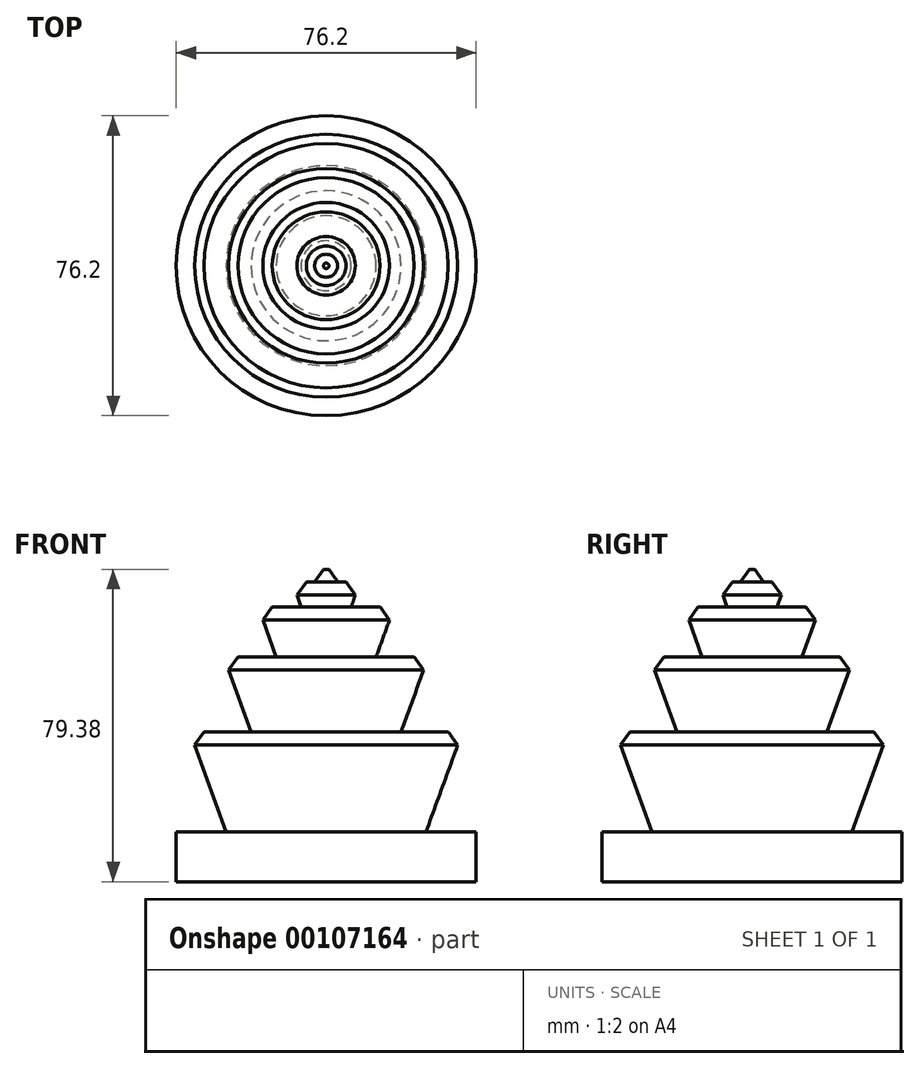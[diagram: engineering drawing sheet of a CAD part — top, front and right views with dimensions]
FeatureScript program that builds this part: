
annotation { "Feature Type Name" : "Feature", "Feature Type Description" : "" }
export const myFeature = defineFeature(function(context is Context, id is Id, definition is map)
    precondition{}
    {
        {
            var Q0;
            Q0=qCreatedBy(makeId("Top.planeOp"),FACE);
            var sketch = newSketch(context, id + "F0", { "sketchPlane" : qUnion([Q0])});
            skCircle(sketch, "E0", {"center": v(0, 0) * mm, "radius": 38.1 * mm});
            skSolve(sketch);
        }
        {
            var Q0;
            Q0 = qSketchRegion(id + "F0", true);
            extrude(context, id + "F1", {"entities" : qUnion([Q0]), "depth" : 12.7 * mm});
        }
        {
            var Q0;
            Q0=makeQuery(id+"F1.opExtrude","CAP_FACE",FACE,{"disambiguationData":[OSD([sQuery(id+"F0.wireOp",EDGE,"E0")])],"isStart":false});
            var sketch = newSketch(context, id + "F2", { "sketchPlane" : qUnion([Q0])});
            skCircle(sketch, "E1", {"center": v(0, 0) * mm, "radius": 25.4 * mm});
            skSolve(sketch);
        }
        {
            var Q0;
            Q0 = qSketchRegion(id + "F2", true);
            extrude(context, id + "F3", {"entities" : qUnion([Q0]), "operationType" : NewBodyOperationType.ADD, "depth" : 25.4 * mm, "hasDraft" : true, "draftAngle" : 20 * degree});
        }
        {
            var Q0;
            Q0=makeQuery(id+"F3.opExtrude","CAP_FACE",FACE,{"disambiguationData":[OSD([sQuery(id+"F2.wireOp",EDGE,"E1")])],"isStart":false});
            var sketch = newSketch(context, id + "F4", { "sketchPlane" : qUnion([Q0])});
            skCircle(sketch, "E2", {"center": v(0, 0) * mm, "radius": 19.05 * mm});
            skSolve(sketch);
        }
        {
            var Q0;
            Q0 = qSketchRegion(id + "F4", true);
            extrude(context, id + "F5", {"entities" : qUnion([Q0]), "operationType" : NewBodyOperationType.ADD, "depth" : 19.05 * mm, "hasDraft" : true, "draftAngle" : 20 * degree});
        }
        {
            var Q0;
            Q0=makeQuery(id+"F5.opExtrude","CAP_FACE",FACE,{"disambiguationData":[OSD([sQuery(id+"F4.wireOp",EDGE,"E2")])],"isStart":false});
            var sketch = newSketch(context, id + "F6", { "sketchPlane" : qUnion([Q0])});
            skCircle(sketch, "E3", {"center": v(0, 0) * mm, "radius": 12.7 * mm});
            skSolve(sketch);
        }
        {
            var Q0;
            Q0 = qSketchRegion(id + "F6", true);
            extrude(context, id + "F7", {"entities" : qUnion([Q0]), "operationType" : NewBodyOperationType.ADD, "depth" : 12.7 * mm, "hasDraft" : true, "draftAngle" : 20 * degree});
        }
        {
            var Q0;
            Q0=makeQuery(id+"F7.opExtrude","CAP_FACE",FACE,{"disambiguationData":[OSD([sQuery(id+"F6.wireOp",EDGE,"E3")])],"isStart":false});
            var sketch = newSketch(context, id + "F8", { "sketchPlane" : qUnion([Q0])});
            skCircle(sketch, "E4", {"center": v(0, 0) * mm, "radius": 6.35 * mm});
            skSolve(sketch);
        }
        {
            var Q0;
            Q0 = qSketchRegion(id + "F8", true);
            extrude(context, id + "F9", {"entities" : qUnion([Q0]), "operationType" : NewBodyOperationType.ADD, "depth" : 6.35 * mm, "hasDraft" : true, "draftAngle" : 20 * degree});
        }
        {
            var Q0;
            Q0=makeQuery(id+"F9.opExtrude","CAP_FACE",FACE,{"disambiguationData":[OSD([sQuery(id+"F8.wireOp",EDGE,"E4")])],"isStart":false});
            var sketch = newSketch(context, id + "F10", { "sketchPlane" : qUnion([Q0])});
            skCircle(sketch, "E5", {"center": v(0, 0) * mm, "radius": 3.18 * mm});
            skSolve(sketch);
        }
        {
            var Q0;
            Q0=makeQuery(id+"F10.imprint","IMPRINT",FACE,{"disambiguationData":[TD([[makeQuery(id+"F10.imprint","IMPRINT",EDGE,{"derivedFrom":sQuery(id+"F10.wireOp",EDGE,"E5")}),1.0]])]});
            extrude(context, id + "F11", {"entities" : qUnion([Q0]), "operationType" : NewBodyOperationType.ADD, "depth" : 3.17 * mm, "hasDraft" : true, "draftAngle" : 20 * degree});
        }
        {
            var Q0;
            Q0=makeQuery(id+"F3.opExtrude","CAP_EDGE",EDGE,{"disambiguationData":[OSD([sQuery(id+"F2.wireOp",EDGE,"E1")])],"isStart":false});
            var Q1;
            Q1=makeQuery(id+"F5.opExtrude","CAP_EDGE",EDGE,{"disambiguationData":[OSD([sQuery(id+"F4.wireOp",EDGE,"E2")])],"isStart":false});
            var Q2;
            Q2=makeQuery(id+"F7.opExtrude","CAP_EDGE",EDGE,{"disambiguationData":[OSD([sQuery(id+"F6.wireOp",EDGE,"E3")])],"isStart":false});
            var Q3;
            Q3=makeQuery(id+"F9.opExtrude","CAP_EDGE",EDGE,{"disambiguationData":[OSD([sQuery(id+"F8.wireOp",EDGE,"E4")])],"isStart":false});
            var Q4;
            Q4=makeQuery(id+"F11.opExtrude","CAP_EDGE",EDGE,{"disambiguationData":[OSD([sQuery(id+"F10.wireOp",EDGE,"E5")])],"isStart":false});
            chamfer(context, id + "F12", {"entities" : qUnion([Q0, Q1, Q2, Q3, Q4]), "width" : 2.54 * mm, "tangentPropagation" : true});
        }
    });
